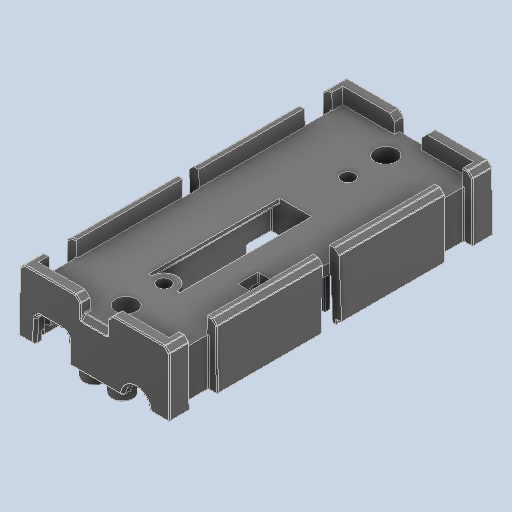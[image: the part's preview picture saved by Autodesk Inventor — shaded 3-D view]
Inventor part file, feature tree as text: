
AUTODESK INVENTOR PART (.ipt)
format: ipt  version: 2024.2 (Build 282272000, 272)  size: 2,767,360 bytes
history: native  units: in
note: dims shown in document units (in); Inventor stores cm internally (conversion verified against a paired STEP export)
features: fillet x1
ambient origin geometry x8: Origin, YZ Plane, XZ Plane, XY Plane, X Axis, Y Axis, Z Axis, Center Point
bodies: Solid1 (feature_tree)
feature tree (1):
  fillet  "Fillet20"  [1 undecoded]
note: 1 required parameter value undecoded (feature->parameter linkage not recoverable at this tier; creation-order binding heuristic only, values carry confidence <= 0.55)
